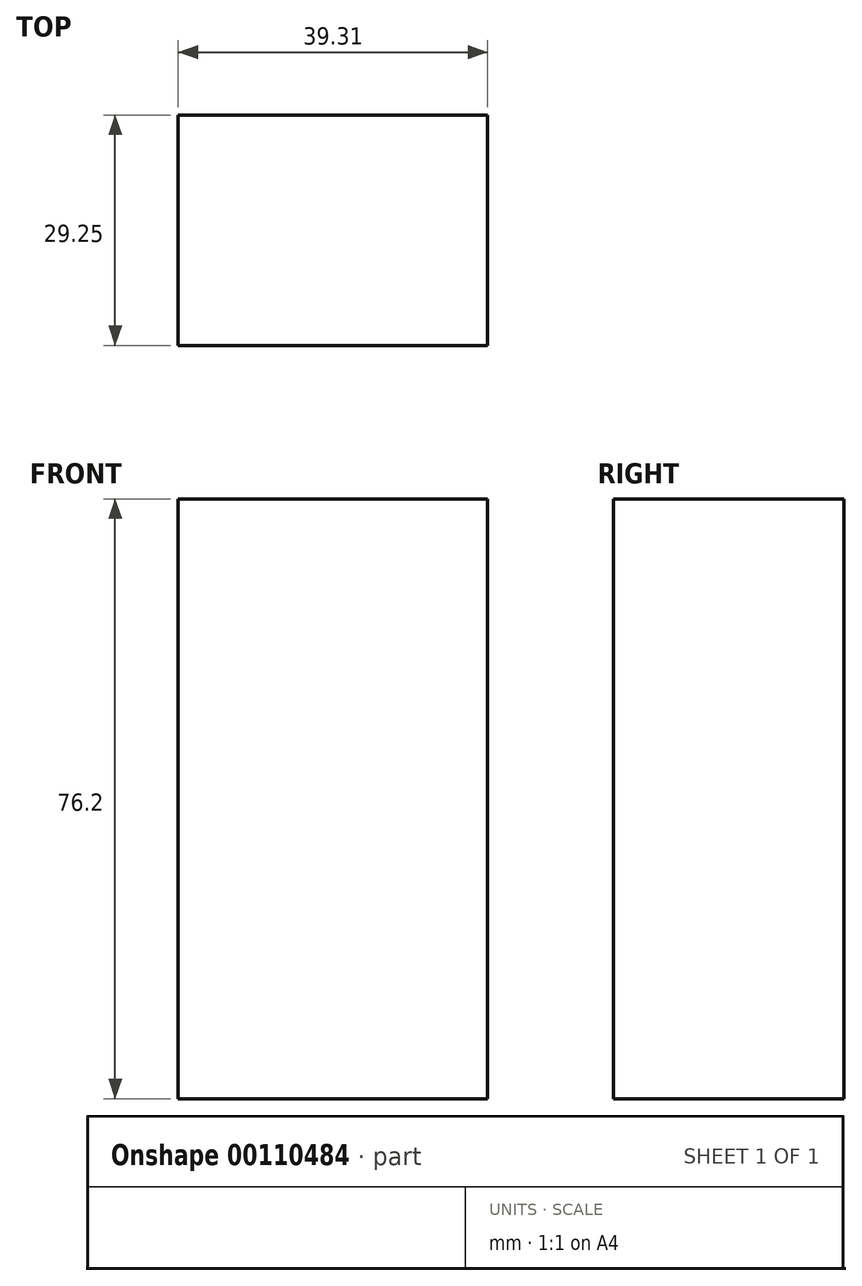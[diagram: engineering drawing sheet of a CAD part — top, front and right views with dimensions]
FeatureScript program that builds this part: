
annotation { "Feature Type Name" : "Feature", "Feature Type Description" : "" }
export const myFeature = defineFeature(function(context is Context, id is Id, definition is map)
    precondition{}
    {
        {
            var Q0;
            Q0=qCreatedBy(makeId("Top.planeOp"),FACE);
            var sketch = newSketch(context, id + "F0", { "sketchPlane" : qUnion([Q0])});
            skLineSegment(sketch, "E0.bottom", {"start": v(0, 0) * mm, "end": v(39.3, 0) * mm});
            skLineSegment(sketch, "E0.top", {"start": v(0, 29.25) * mm, "end": v(39.3, 29.25) * mm});
            skLineSegment(sketch, "E0.left", {"start": v(0, 0) * mm, "end": v(0, 29.25) * mm});
            skLineSegment(sketch, "E0.right", {"start": v(39.3, 0) * mm, "end": v(39.3, 29.25) * mm});
            skSolve(sketch);
        }
        {
            var Q0;
            Q0=makeQuery(id+"F0.imprint","IMPRINT",FACE,{"disambiguationData":[TD([[makeQuery(id+"F0.imprint","IMPRINT",EDGE,{"derivedFrom":sQuery(id+"F0.wireOp",EDGE,"E0.bottom")}),1.0]])]});
            extrude(context, id + "F1", {"entities" : qUnion([Q0]), "endBound" : BoundingType.SYMMETRIC, "depth" : 76.2 * mm});
        }
    });
